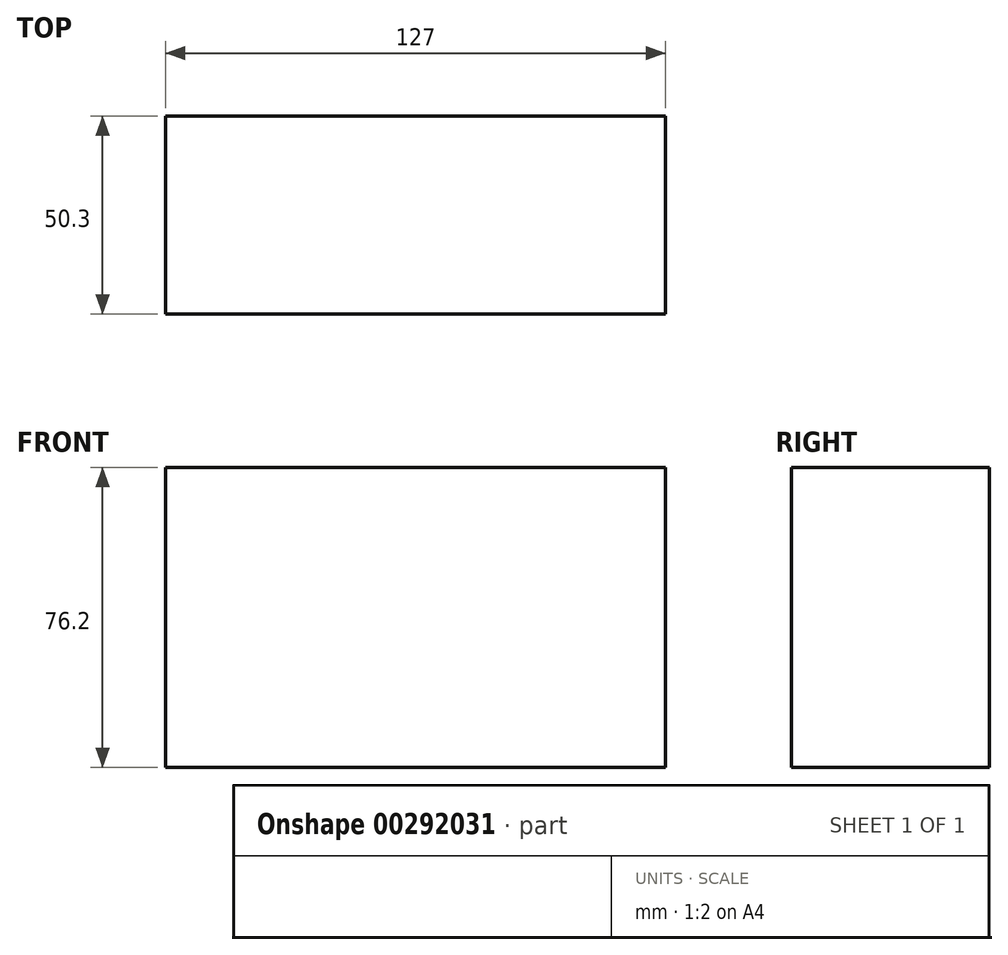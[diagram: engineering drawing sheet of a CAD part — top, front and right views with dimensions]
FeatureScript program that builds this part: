
annotation { "Feature Type Name" : "Feature", "Feature Type Description" : "" }
export const myFeature = defineFeature(function(context is Context, id is Id, definition is map)
    precondition{}
    {
        {
            var Q0;
            Q0=qCreatedBy(makeId("Top.planeOp"),FACE);
            var sketch = newSketch(context, id + "F0", { "sketchPlane" : qUnion([Q0])});
            skLineSegment(sketch, "E0.bottom", {"start": v(-45.15, 58.14) * mm, "end": v(81.85, 58.14) * mm});
            skLineSegment(sketch, "E0.top", {"start": v(-45.15, 7.84) * mm, "end": v(81.85, 7.84) * mm});
            skLineSegment(sketch, "E0.left", {"start": v(-45.15, 58.14) * mm, "end": v(-45.15, 7.84) * mm});
            skLineSegment(sketch, "E0.right", {"start": v(81.85, 58.14) * mm, "end": v(81.85, 7.84) * mm});
            skSolve(sketch);
        }
        {
            var Q0;
            Q0=makeQuery(id+"F0.imprint","IMPRINT",FACE,{"disambiguationData":[TD([[makeQuery(id+"F0.imprint","IMPRINT",EDGE,{"derivedFrom":sQuery(id+"F0.wireOp",EDGE,"E0.bottom")}),-1.0]])]});
            extrude(context, id + "F1", {"entities" : qUnion([Q0]), "oppositeDirection" : true, "depth" : 76.2 * mm});
        }
    });
